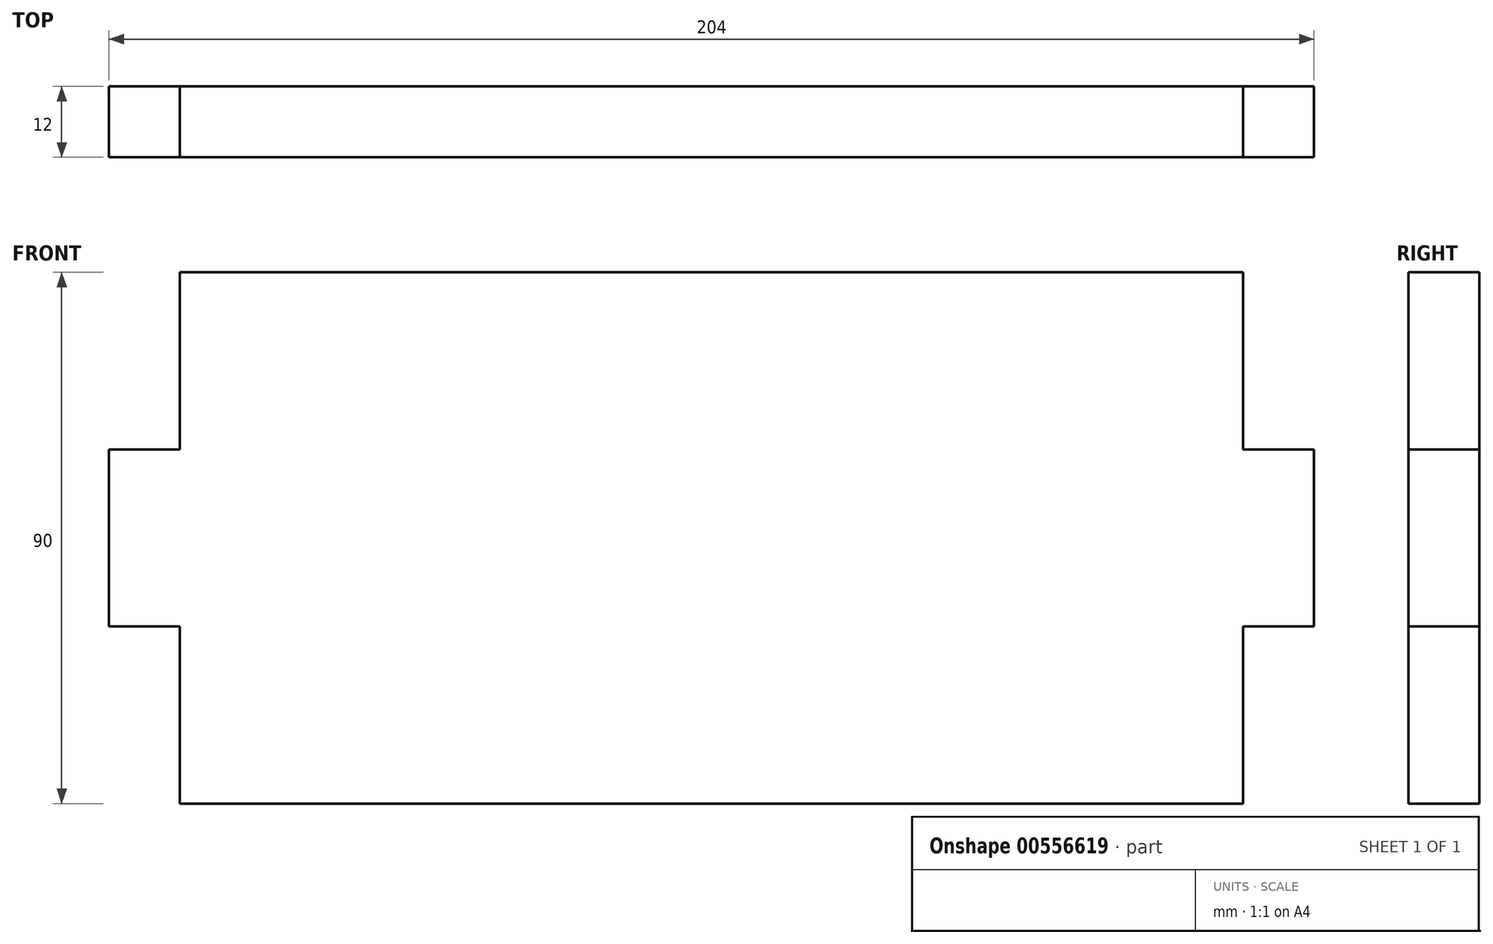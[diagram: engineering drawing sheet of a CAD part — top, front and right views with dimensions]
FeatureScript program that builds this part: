
annotation { "Feature Type Name" : "Feature", "Feature Type Description" : "" }
export const myFeature = defineFeature(function(context is Context, id is Id, definition is map)
    precondition{}
    {
        {
            var Q0;
            Q0=qCreatedBy(makeId("Front.planeOp"),FACE);
            var sketch = newSketch(context, id + "F0", { "sketchPlane" : qUnion([Q0])});
            skLineSegment(sketch, "E0", {"start": v(0, 0) * mm, "end": v(0, 30) * mm});
            skLineSegment(sketch, "E1", {"start": v(0, 30) * mm, "end": v(-12, 30) * mm});
            skLineSegment(sketch, "E2", {"start": v(-12, 30) * mm, "end": v(-12, 60) * mm});
            skLineSegment(sketch, "E3", {"start": v(-12, 60) * mm, "end": v(0, 60) * mm});
            skLineSegment(sketch, "E4", {"start": v(0, 60) * mm, "end": v(0, 90) * mm});
            skLineSegment(sketch, "E5", {"start": v(0, 90) * mm, "end": v(90, 90) * mm});
            skLineSegment(sketch, "E6", {"start": v(90, 90) * mm, "end": v(90, 0) * mm});
            skLineSegment(sketch, "E7", {"start": v(90, 0) * mm, "end": v(0, 0) * mm});
            skLineSegment(sketch, "E8.MirrorCS", {"start": v(180, 30) * mm, "end": v(192, 30) * mm});
            skLineSegment(sketch, "E9.MirrorCS", {"start": v(180, 0) * mm, "end": v(180, 30) * mm});
            skLineSegment(sketch, "E10.MirrorCS", {"start": v(192, 30) * mm, "end": v(192, 60) * mm});
            skLineSegment(sketch, "E11.MirrorCS", {"start": v(192, 60) * mm, "end": v(180, 60) * mm});
            skLineSegment(sketch, "E12.MirrorCS", {"start": v(180, 90) * mm, "end": v(90, 90) * mm});
            skLineSegment(sketch, "E13.MirrorCS", {"start": v(180, 60) * mm, "end": v(180, 90) * mm});
            skLineSegment(sketch, "E14.MirrorCS", {"start": v(90, 0) * mm, "end": v(180, 0) * mm});
            skSolve(sketch);
        }
        {
            var Q0;
            Q0=makeQuery(id+"F0.imprint","IMPRINT",FACE,{"disambiguationData":[TD([[makeQuery(id+"F0.imprint","IMPRINT",EDGE,{"derivedFrom":sQuery(id+"F0.wireOp",EDGE,"E6")}),1.0]])]});
            var Q1;
            Q1=makeQuery(id+"F0.imprint","IMPRINT",FACE,{"disambiguationData":[TD([[makeQuery(id+"F0.imprint","IMPRINT",EDGE,{"derivedFrom":sQuery(id+"F0.wireOp",EDGE,"E0")}),-1.0]])]});
            extrude(context, id + "F1", {"entities" : qUnion([Q0, Q1]), "endBound" : BoundingType.SYMMETRIC, "depth" : 12 * mm, "offsetDistance" : 25 * mm});
        }
    });
